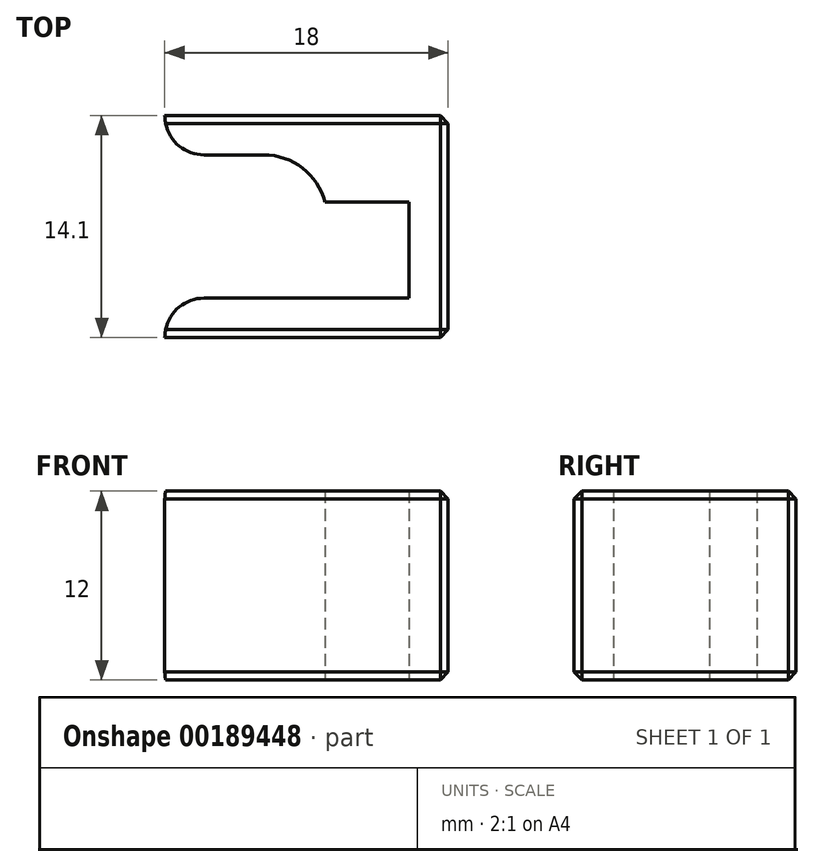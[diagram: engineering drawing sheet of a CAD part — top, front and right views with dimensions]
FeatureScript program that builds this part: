
annotation { "Feature Type Name" : "Feature", "Feature Type Description" : "" }
export const myFeature = defineFeature(function(context is Context, id is Id, definition is map)
    precondition{}
    {
        {
            var Q0;
            Q0=qCreatedBy(makeId("Top.planeOp"),FACE);
            var sketch = newSketch(context, id + "F0", { "sketchPlane" : qUnion([Q0])});
            skLineSegment(sketch, "E0.bottom", {"start": v(-9, 7.05) * mm, "end": v(9, 7.05) * mm});
            skLineSegment(sketch, "E0.top", {"start": v(-9, -7.05) * mm, "end": v(9, -7.05) * mm});
            skLineSegment(sketch, "E0.right", {"start": v(9, 7.05) * mm, "end": v(9, -7.05) * mm});
            skPoint(sketch, "E0.middle", {"position": v(0, 0) * mm});
            skLineSegment(sketch, "E1", {"start": v(6.5, 1.55) * mm, "end": v(6.5, -4.55) * mm});
            skLineSegment(sketch, "E2", {"start": v(6.5, -4.55) * mm, "end": v(-6.5, -4.55) * mm});
            skArc(sketch, "E3", {"start": v(-9, 7.05) * mm, "mid": v(-8.27, 5.28) * mm, "end": v(-6.5, 4.55) * mm});
            skArc(sketch, "E4.MirrorCS", {"start": v(-9, -7.05) * mm, "mid": v(-8.27, -5.28) * mm, "end": v(-6.5, -4.55) * mm});
            skLineSegment(sketch, "E5", {"start": v(-6.5, 4.55) * mm, "end": v(-2.7, 4.55) * mm});
            skLineSegment(sketch, "E6", {"start": v(6.5, 1.55) * mm, "end": v(1.17, 1.55) * mm});
            skArc(sketch, "E7", {"start": v(1.17, 1.55) * mm, "mid": v(-0.26, 3.71) * mm, "end": v(-2.7, 4.55) * mm});
            skSolve(sketch);
        }
        {
            var Q0;
            {var subQ3=sQuery(id+"F0.wireOp",EDGE,"E0.bottom");Q0=makeQuery(id+"F0.imprint","IMPRINT",FACE,{"disambiguationData":[TD([[makeQuery(id+"F0.imprint","IMPRINT",EDGE,{"derivedFrom":subQ3}),-1.0]])]});}
            extrude(context, id + "F1", {"entities" : qUnion([Q0]), "endBound" : BoundingType.SYMMETRIC, "depth" : 12 * mm});
        }
        {
            var Q0;
            Q0=makeQuery(id+"F1.opExtrude","SWEPT_EDGE",EDGE,{"disambiguationData":[OSD([sQuery(id+"F0.wireOp",EDGE,"E0.bottom"),sQuery(id+"F0.wireOp",EDGE,"E0.right")])]});
            var Q1;
            Q1=makeQuery(id+"F1.opExtrude","SWEPT_EDGE",EDGE,{"disambiguationData":[OSD([sQuery(id+"F0.wireOp",EDGE,"E0.top"),sQuery(id+"F0.wireOp",EDGE,"E0.right")])]});
            var Q2;
            Q2=makeQuery(id+"F1.opExtrude","CAP_EDGE",EDGE,{"disambiguationData":[OSD([sQuery(id+"F0.wireOp",EDGE,"E0.right")])],"isStart":false});
            var Q3;
            Q3=makeQuery(id+"F1.opExtrude","CAP_EDGE",EDGE,{"disambiguationData":[OSD([sQuery(id+"F0.wireOp",EDGE,"E0.right")])],"isStart":true});
            var Q4;
            Q4=makeQuery(id+"F1.opExtrude","CAP_EDGE",EDGE,{"disambiguationData":[OSD([sQuery(id+"F0.wireOp",EDGE,"E0.bottom")])],"isStart":true});
            var Q5;
            Q5=makeQuery(id+"F1.opExtrude","CAP_EDGE",EDGE,{"disambiguationData":[OSD([sQuery(id+"F0.wireOp",EDGE,"E0.bottom")])],"isStart":false});
            var Q6;
            Q6=makeQuery(id+"F1.opExtrude","CAP_EDGE",EDGE,{"disambiguationData":[OSD([sQuery(id+"F0.wireOp",EDGE,"E0.top")])],"isStart":false});
            var Q7;
            Q7=makeQuery(id+"F1.opExtrude","CAP_EDGE",EDGE,{"disambiguationData":[OSD([sQuery(id+"F0.wireOp",EDGE,"E0.top")])],"isStart":true});
            chamfer(context, id + "F2", {"entities" : qUnion([Q0, Q1, Q2, Q3, Q4, Q5, Q6, Q7]), "width" : .5 * mm, "tangentPropagation" : true});
        }
        {
            var Q0;
            Q0=makeQuery(id+"F1.opExtrude","SWEPT_BODY",BODY,{"disambiguationData":[OSD([sQuery(id+"F0.wireOp",EDGE,"E0.bottom"),sQuery(id+"F0.wireOp",EDGE,"E0.top"),sQuery(id+"F0.wireOp",EDGE,"E0.right"),sQuery(id+"F0.wireOp",EDGE,"E1"),sQuery(id+"F0.wireOp",EDGE,"E2"),sQuery(id+"F0.wireOp",EDGE,"E3"),sQuery(id+"F0.wireOp",EDGE,"E4.MirrorCS"),sQuery(id+"F0.wireOp",EDGE,"E5"),sQuery(id+"F0.wireOp",EDGE,"E6"),sQuery(id+"F0.wireOp",EDGE,"E7")])]});
            transform(context, id + "F3", {"entities" : qUnion([Q0]), "transformType" : TransformType.TRANSLATION_3D, "dx" : 26.4 * mm, "dy" : 0 * mm, "dz" : 0 * mm, "makeCopy" : true});
        }
        {
            var Q0;
            Q0=makeQuery(id+"F3.opPattern","COPY",BODY,{"derivedFrom":makeQuery(id+"F1.opExtrude","SWEPT_BODY",BODY,{"disambiguationData":[OSD([sQuery(id+"F0.wireOp",EDGE,"E0.bottom"),sQuery(id+"F0.wireOp",EDGE,"E0.top"),sQuery(id+"F0.wireOp",EDGE,"E0.right"),sQuery(id+"F0.wireOp",EDGE,"E1"),sQuery(id+"F0.wireOp",EDGE,"E2"),sQuery(id+"F0.wireOp",EDGE,"E3"),sQuery(id+"F0.wireOp",EDGE,"E4.MirrorCS"),sQuery(id+"F0.wireOp",EDGE,"E5"),sQuery(id+"F0.wireOp",EDGE,"E6"),sQuery(id+"F0.wireOp",EDGE,"E7")])]}),"instanceName":"1"});
            deleteBodies(context, id + "F4", {"entities" : qUnion([Q0])});
        }
    });
